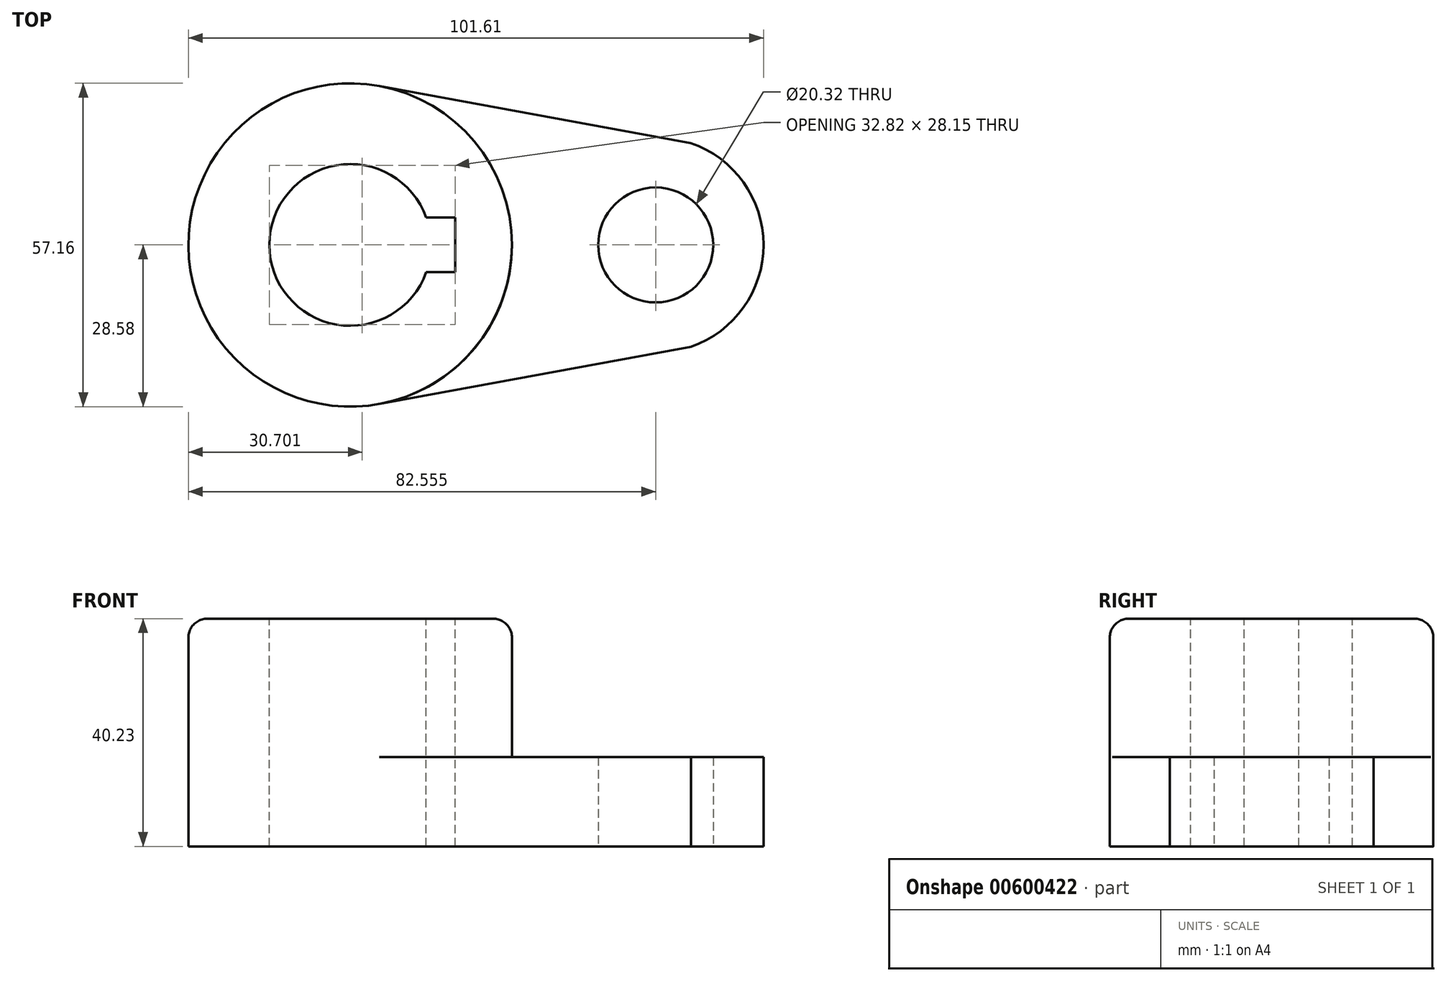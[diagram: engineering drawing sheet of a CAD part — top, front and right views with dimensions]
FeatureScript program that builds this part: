
annotation { "Feature Type Name" : "Feature", "Feature Type Description" : "" }
export const myFeature = defineFeature(function(context is Context, id is Id, definition is map)
    precondition{}
    {
        {
            var Q0;
            Q0=qCreatedBy(makeId("Top.planeOp"),FACE);
            var sketch = newSketch(context, id + "F0", { "sketchPlane" : qUnion([Q0])});
            skArc(sketch, "E0", {"start": v(5.15, 28.1) * mm, "mid": v(-28.57, 0) * mm, "end": v(5.16, -28.1) * mm});
            skArc(sketch, "E1", {"start": v(60.22, -18) * mm, "mid": v(73.02, 0.03) * mm, "end": v(60.16, 18.02) * mm});
            skLineSegment(sketch, "E2", {"start": v(0, 0) * mm, "end": v(53.97, 0) * mm, "construction": true});
            skLineSegment(sketch, "E3", {"start": v(60.16, 18.02) * mm, "end": v(5.15, 28.1) * mm});
            skLineSegment(sketch, "E4", {"start": v(60.22, -18) * mm, "end": v(5.16, -28.1) * mm});
            skCircle(sketch, "E5", {"center": v(53.97, 0) * mm, "radius": 10.16 * mm});
            skSolve(sketch);
        }
        {
            var Q0;
            Q0 = qSketchRegion(id + "F0", true);
            extrude(context, id + "F1", {"entities" : qUnion([Q0]), "depth" : (0.62 * 25.4) * mm, "offsetDistance" : 25 * mm});
        }
        {
            var Q0;
            Q0=makeQuery(id+"F1.opExtrude","CAP_FACE",FACE,{"disambiguationData":[OSD([sQuery(id+"F0.wireOp",EDGE,"E0"),sQuery(id+"F0.wireOp",EDGE,"E1"),sQuery(id+"F0.wireOp",EDGE,"E3"),sQuery(id+"F0.wireOp",EDGE,"E4")])],"isStart":false});
            var sketch = newSketch(context, id + "F2", { "sketchPlane" : qUnion([Q0])});
            skCircle(sketch, "E6", {"center": v(0, 0) * mm, "radius": 28.57 * mm});
            skSolve(sketch);
        }
        {
            var Q0;
            {var subQ0=sQuery(id+"F2.wireOp",EDGE,"E6");var subQ1=makeQuery(id+"F2.imprint","INTERSECT",VERTEX,{"derivedFrom":[makeQuery(id+"F1.opExtrude","CAP_EDGE",EDGE,{"disambiguationData":[OSD([sQuery(id+"F0.wireOp",EDGE,"E3")])],"isStart":false}),subQ0]});Q0=makeQuery(id+"F2.imprint","IMPRINT",FACE,{"disambiguationData":[TD([[makeQuery(id+"F2.imprint","IMPRINT",EDGE,{"disambiguationData":[TD([[subQ1,-1.0]])],"derivedFrom":subQ0}),1.0]])]});}
            extrude(context, id + "F3", {"entities" : qUnion([Q0]), "operationType" : NewBodyOperationType.ADD, "depth" : ((1.58 - 0.62) * 25.4) * mm, "offsetDistance" : 25 * mm});
        }
        {
            var Q0;
            Q0=makeQuery(id+"F3.opExtrude","CAP_FACE",FACE,{"disambiguationData":[OSD([sQuery(id+"F2.wireOp",EDGE,"E6")])],"isStart":false});
            var sketch = newSketch(context, id + "F4", { "sketchPlane" : qUnion([Q0])});
            skArc(sketch, "E7", {"start": v(13.45, 4.83) * mm, "mid": v(-14.29, 0) * mm, "end": v(13.45, -4.83) * mm});
            skLineSegment(sketch, "E8.bottom", {"start": v(18.53, -4.83) * mm, "end": v(13.45, -4.83) * mm});
            skLineSegment(sketch, "E8.top", {"start": v(18.53, 4.83) * mm, "end": v(13.45, 4.83) * mm});
            skLineSegment(sketch, "E8.left", {"start": v(18.53, -4.83) * mm, "end": v(18.53, 4.83) * mm});
            skSolve(sketch);
        }
        {
            var Q0;
            Q0=makeQuery(id+"F4.imprint","IMPRINT",FACE,{"disambiguationData":[TD([[makeQuery(id+"F4.imprint","IMPRINT",EDGE,{"derivedFrom":sQuery(id+"F4.wireOp",EDGE,"E7")}),1.0]])]});
            extrude(context, id + "F5", {"entities" : qUnion([Q0]), "operationType" : NewBodyOperationType.REMOVE, "endBound" : BoundingType.THROUGH_ALL, "oppositeDirection" : true, "depth" : (1.58 * 25.4) * mm, "offsetDistance" : 25 * mm});
        }
        {
            var Q0;
            Q0=makeQuery(id+"F3.opExtrude","CAP_EDGE",EDGE,{"disambiguationData":[OSD([sQuery(id+"F2.wireOp",EDGE,"E6")])],"isStart":false});
            fillet(context, id + "F6", {"entities" : qUnion([Q0]), "radius" : (0.13 * 25.4) * mm, "tangentPropagation" : true, "allowEdgeOverflow" : false});
        }
    });
